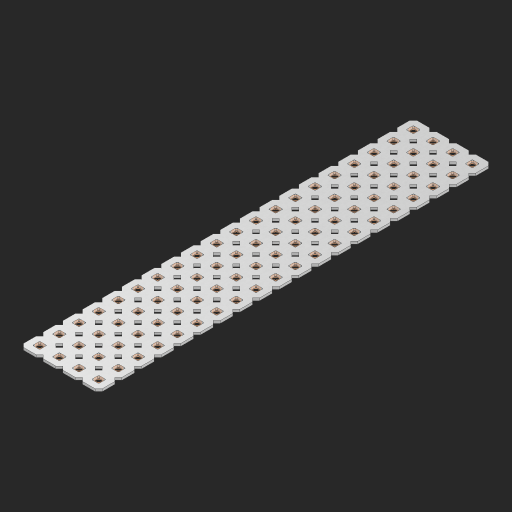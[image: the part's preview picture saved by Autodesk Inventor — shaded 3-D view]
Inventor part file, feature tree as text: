
AUTODESK INVENTOR PART (.ipt)
format: ipt  version: 2023 (Build 270158000, 158)  size: 1,204,736 bytes
history: native  units: in
note: dims shown in document units (in); Inventor stores cm internally (conversion verified against a paired STEP export)
features: other x81, extrude x79, sketch x2, pattern_linear x1
ambient origin geometry x8: Origin, YZ Plane, XZ Plane, XY Plane, X Axis, Y Axis, Z Axis, Center Point
bodies: Solid1 (feature_tree), Body (feature_tree)
feature tree (163):
  pattern_linear  "Rectangular Pattern1"  Spacing1=0.09in  [1 undecoded]
  sketch  "Sketch1"  dims[d1=0.5in]
  sketch  "Sketch2"  dims[d2=0.182in d3=0.09in d4=0.09in d5=0.09in d6=0.09in d7=0.09in d8=0.09in d9=0.09in d10=0.09in d11=0.02in d13=0.0in d14=0.172in d15=0.0625in d16=0.0in d19=0.5in d22=0.5in]
  other  "Srf1"
  other  "Srf126"
  other  "Srf127"
  other  "Srf128"
  other  "Srf129"
  other  "Srf130"
  other  "Srf131"
  other  "Srf250"
  other  "Srf251"
  other  "Srf252"
  other  "Srf253"
  other  "Srf254"
  other  "Srf255"
  other  "Srf256"
  other  "Srf257"
  other  "Srf258"
  other  "Srf259"
  other  "Srf260"
  other  "Srf261"
  other  "Srf262"
  other  "Srf268"
  other  "Srf269"
  other  "Srf270"
  other  "Srf271"
  other  "Srf272"
  other  "Srf273"
  other  "Srf274"
  other  "Srf275"
  other  "Srf276"
  other  "Srf277"
  other  "Srf278"
  other  "Srf279"
  other  "Srf280"
  other  "Srf281"
  other  "Srf282"
  other  "Srf283"
  other  "Srf284"
  other  "Srf285"
  other  "Srf286"
  other  "Srf287"
  other  "Srf293"
  other  "Srf294"
  other  "Srf295"
  other  "Srf296"
  other  "Srf297"
  other  "Srf298"
  other  "Srf299"
  other  "Srf300"
  other  "Srf301"
  other  "Srf302"
  other  "Srf303"
  other  "Srf304"
  other  "Srf305"
  other  "Srf306"
  other  "Srf307"
  other  "Srf308"
  other  "Srf309"
  other  "Srf310"
  other  "Srf311"
  other  "Srf312"
  other  "Srf318"
  other  "Srf319"
  other  "Srf320"
  other  "Srf321"
  other  "Srf322"
  other  "Srf323"
  other  "Srf324"
  other  "Srf325"
  other  "Srf326"
  other  "Srf327"
  other  "Srf328"
  other  "Srf329"
  other  "Srf330"
  other  "Srf331"
  other  "Srf332"
  other  "Srf333"
  other  "Srf334"
  other  "Srf335"
  other  "Srf336"
  other  "Srf337"
  other  "Circle"
  extrude  "ExtrusionSrf126"  Depth=0.09in
  extrude  "ExtrusionSrf127"  Depth=0.09in
  extrude  "ExtrusionSrf128"  Depth=0.09in
  extrude  "ExtrusionSrf129"  Depth=0.09in
  extrude  "ExtrusionSrf130"  Depth=0.09in
  extrude  "ExtrusionSrf131"  Depth=0.09in
  extrude  "ExtrusionSrf250"  Depth=0.09in
  extrude  "ExtrusionSrf251"  Depth=0.02in
  extrude  "ExtrusionSrf252"  TaperAngle=0.0deg  [1 undecoded]
  extrude  "ExtrusionSrf253"  Depth=0.5in
  extrude  "ExtrusionSrf254"  Depth=0.0625in TaperAngle=0.0deg
  extrude  "ExtrusionSrf255"  Depth=0.5in
  extrude  "ExtrusionSrf256"  Depth=0.5in
  extrude  "ExtrusionSrf257"  [1 undecoded]
  extrude  "ExtrusionSrf258"  [1 undecoded]
  extrude  "ExtrusionSrf259"  [1 undecoded]
  extrude  "ExtrusionSrf260"  [1 undecoded]
  extrude  "ExtrusionSrf261"  [1 undecoded]
  extrude  "ExtrusionSrf262"  [1 undecoded]
  extrude  "ExtrusionSrf268"  [1 undecoded]
  extrude  "ExtrusionSrf269"  [1 undecoded]
  extrude  "ExtrusionSrf270"  [1 undecoded]
  extrude  "ExtrusionSrf271"  [1 undecoded]
  extrude  "ExtrusionSrf272"  [1 undecoded]
  extrude  "ExtrusionSrf273"  [1 undecoded]
  extrude  "ExtrusionSrf274"  [1 undecoded]
  extrude  "ExtrusionSrf275"  [1 undecoded]
  extrude  "ExtrusionSrf276"  [1 undecoded]
  extrude  "ExtrusionSrf277"  [1 undecoded]
  extrude  "ExtrusionSrf278"  [1 undecoded]
  extrude  "ExtrusionSrf279"  [1 undecoded]
  extrude  "ExtrusionSrf280"  [1 undecoded]
  extrude  "ExtrusionSrf281"  [1 undecoded]
  extrude  "ExtrusionSrf282"  [1 undecoded]
  extrude  "ExtrusionSrf283"  [1 undecoded]
  extrude  "ExtrusionSrf284"  [1 undecoded]
  extrude  "ExtrusionSrf285"  [1 undecoded]
  extrude  "ExtrusionSrf286"  [1 undecoded]
  extrude  "ExtrusionSrf287"  [1 undecoded]
  extrude  "ExtrusionSrf293"  [1 undecoded]
  extrude  "ExtrusionSrf294"  [1 undecoded]
  extrude  "ExtrusionSrf295"  [1 undecoded]
  extrude  "ExtrusionSrf296"  [1 undecoded]
  extrude  "ExtrusionSrf297"  [1 undecoded]
  extrude  "ExtrusionSrf298"  [1 undecoded]
  extrude  "ExtrusionSrf299"  [1 undecoded]
  extrude  "ExtrusionSrf300"  [1 undecoded]
  extrude  "ExtrusionSrf301"  [1 undecoded]
  extrude  "ExtrusionSrf302"  [1 undecoded]
  extrude  "ExtrusionSrf303"  [1 undecoded]
  extrude  "ExtrusionSrf304"  [1 undecoded]
  extrude  "ExtrusionSrf305"  [1 undecoded]
  extrude  "ExtrusionSrf306"  [1 undecoded]
  extrude  "ExtrusionSrf307"  [1 undecoded]
  extrude  "ExtrusionSrf308"  [1 undecoded]
  extrude  "ExtrusionSrf309"  [1 undecoded]
  extrude  "ExtrusionSrf310"  [1 undecoded]
  extrude  "ExtrusionSrf311"  [1 undecoded]
  extrude  "ExtrusionSrf312"  [1 undecoded]
  extrude  "ExtrusionSrf318"  [1 undecoded]
  extrude  "ExtrusionSrf319"  [1 undecoded]
  extrude  "ExtrusionSrf320"  [1 undecoded]
  extrude  "ExtrusionSrf321"  [1 undecoded]
  extrude  "ExtrusionSrf322"  [1 undecoded]
  extrude  "ExtrusionSrf323"  [1 undecoded]
  extrude  "ExtrusionSrf324"  [1 undecoded]
  extrude  "ExtrusionSrf325"  [1 undecoded]
  extrude  "ExtrusionSrf326"  [1 undecoded]
  extrude  "ExtrusionSrf327"  [1 undecoded]
  extrude  "ExtrusionSrf328"  [1 undecoded]
  extrude  "ExtrusionSrf329"  [1 undecoded]
  extrude  "ExtrusionSrf330"  [1 undecoded]
  extrude  "ExtrusionSrf331"  [1 undecoded]
  extrude  "ExtrusionSrf332"  [1 undecoded]
  extrude  "ExtrusionSrf333"  [1 undecoded]
  extrude  "ExtrusionSrf334"  [1 undecoded]
  extrude  "ExtrusionSrf335"  [1 undecoded]
  extrude  "ExtrusionSrf336"  [1 undecoded]
  extrude  "ExtrusionSrf337"  [1 undecoded]
note: 68 required parameter values undecoded (feature->parameter linkage not recoverable at this tier; creation-order binding heuristic only, values carry confidence <= 0.55)
